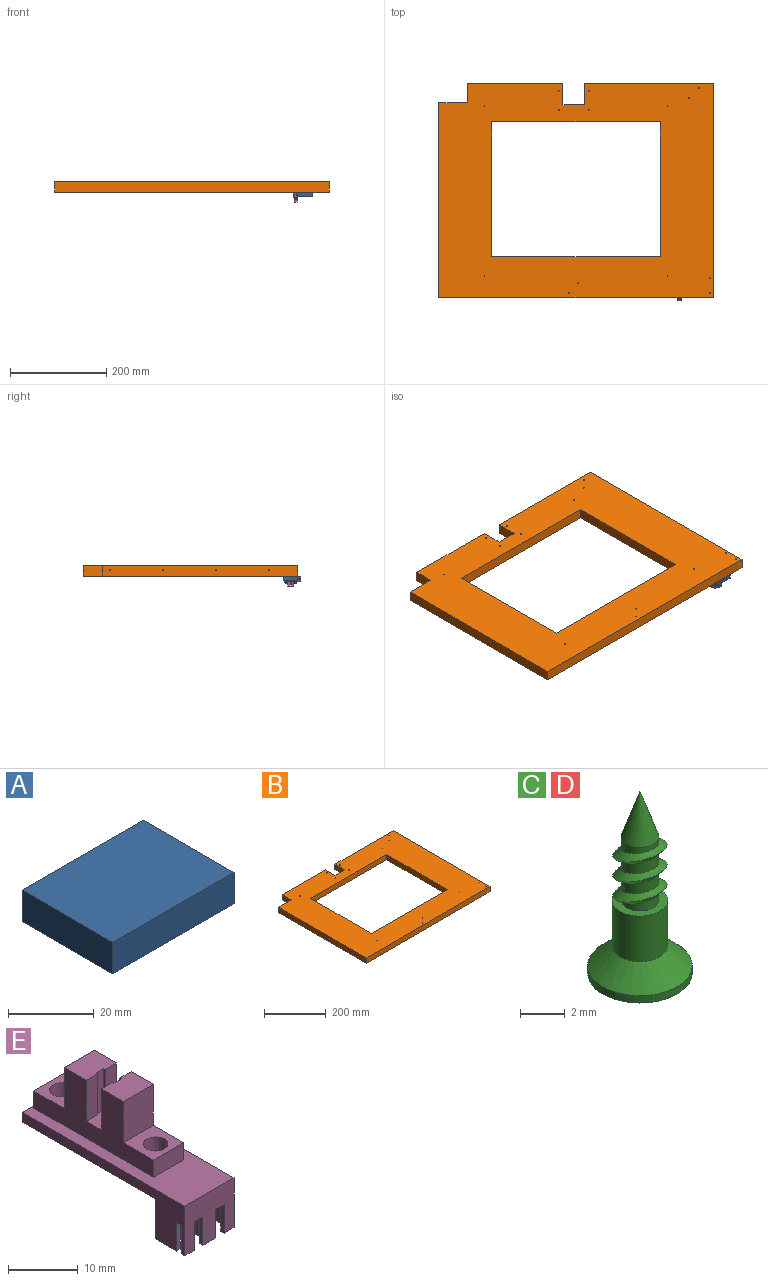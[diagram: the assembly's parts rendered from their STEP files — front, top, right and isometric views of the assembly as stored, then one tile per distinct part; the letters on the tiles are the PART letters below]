
ASSEMBLY  parts=5 mates=4
PART A: 6 faces, bbox 40x30x9 mm
  f0: plane 40x9mm, normal (0,-1,0), area 360mm2, adj f1,f3,f4,f5
  f1: plane 30x9mm, normal (-1,0,0), area 270mm2, adj f0,f2,f4,f5
  f2: plane 40x9mm, normal (0,1,0), area 360mm2, adj f1,f3,f4,f5
  f3: plane 30x9mm, normal (1,0,0), area 270mm2, adj f0,f2,f4,f5
  f4: plane 40x30mm, normal (0,0,-1), area 1200mm2, adj f0,f1,f2,f3
  f5: plane 40x30mm, normal (0,0,1), area 1200mm2, adj f0,f1,f2,f3
PART B: 72 faces, bbox 570x445x21 mm
  f0: plane 198x21mm, normal (0,1,0), area 4154.9mm2, adj f1,f2,f24,f25,f62
  f1: plane 570x445mm, normal (0,0,1), area 151270mm2, adj f0,f9,f10,f11,f12,f13,f14,f15
  f2: plane 570x445mm, normal (0,0,-1), area 149931.7mm2, adj f0,f3,f4,f5,f6,f7,f8,f9
  f3: cylinder r=8mm len=16mm, axis (0,0,-1), area 552.9mm2, adj f2,f21
  f4: cylinder r=5mm len=11mm, axis (0,0,-1), area 345.6mm2, adj f2,f20
  f5: cylinder r=8mm len=16mm, axis (0,0,-1), area 552.9mm2, adj f2,f19
  f6: cylinder r=8mm len=16mm, axis (0,0,-1), area 552.9mm2, adj f2,f18
  f7: cylinder r=5mm len=11mm, axis (0,0,-1), area 345.6mm2, adj f2,f17
  f8: cylinder r=8mm len=16mm, axis (0,0,-1), area 552.9mm2, adj f2,f16
  f9: plane 570x21mm, normal (0,-1,0), area 11970mm2, adj f1,f2,f14,f15
  f10: plane 280x21mm, normal (1,0,0), area 5880mm2, adj f1,f2,f11,f13
  f11: plane 350x21mm, normal (0,-1,0), area 7350mm2, adj f1,f2,f10,f12
  f12: plane 280x21mm, normal (-1,0,0), area 5880mm2, adj f1,f2,f11,f13
  f13: plane 350x21mm, normal (0,1,0), area 7350mm2, adj f1,f2,f10,f12
  f14: plane 405x21mm, normal (-1,0,0), area 8492.4mm2, adj f1,f2,f9,f23,f50,f52,f54,f56
  f15: plane 445x21mm, normal (1,0,0), area 9332.4mm2, adj f1,f2,f9,f22,f42,f44,f46,f48
  f16: plane 16x16mm, normal (0,0,-1), area 201.1mm2, adj f8
  f17: plane 10x10mm, normal (0,0,-1), area 78.5mm2, adj f7
  f18: plane 16x16mm, normal (0,0,-1), area 201.1mm2, adj f6
  f19: plane 16x16mm, normal (0,0,-1), area 201.1mm2, adj f5
  f20: plane 10x10mm, normal (0,0,-1), area 78.5mm2, adj f4
  f21: plane 16x16mm, normal (0,0,-1), area 201.1mm2, adj f3
  f22: plane 268x21mm, normal (0,1,0), area 5621.7mm2, adj f1,f2,f15,f27,f58,f60
  f23: plane 60x21mm, normal (0,1,0), area 1260mm2, adj f1,f2,f14,f24
  f24: plane 40x21mm, normal (-1,0,0), area 840mm2, adj f0,f1,f2,f23
  f25: plane 44x21mm, normal (1,0,0), area 924mm2, adj f0,f1,f2,f26
  f26: plane 44x21mm, normal (0,1,0), area 924mm2, adj f1,f2,f25,f27
  f27: plane 44x21mm, normal (-1,0,0), area 924mm2, adj f1,f2,f22,f26
  f28: cylinder r=1mm len=21mm, axis (0,0,-1), area 131.9mm2, adj f1,f2
  f29: cylinder r=1mm len=18mm, axis (0,0,-1), area 113.1mm2, adj f1,f69
  f30: cylinder r=1mm len=18mm, axis (0,0,-1), area 113.1mm2, adj f1,f68
  f31: cylinder r=1mm len=18mm, axis (0,0,-1), area 113.1mm2, adj f1,f64
  f32: cylinder r=1mm len=21mm, axis (0,0,-1), area 131.9mm2, adj f1,f2
  f33: cylinder r=1mm len=21mm, axis (0,0,-1), area 131.9mm2, adj f1,f2
  f34: cylinder r=1mm len=21mm, axis (0,0,-1), area 131.9mm2, adj f1,f2
  f35: cylinder r=1mm len=21mm, axis (0,0,-1), area 131.9mm2, adj f1,f2
  f36: cylinder r=1mm len=21mm, axis (0,0,-1), area 131.9mm2, adj f1,f2
  f37: cylinder r=1mm len=18mm, axis (0,0,-1), area 113.1mm2, adj f1,f66
  f38: cylinder r=1mm len=18mm, axis (0,0,-1), area 113.1mm2, adj f1,f65
  f39: cylinder r=1mm len=18mm, axis (0,0,-1), area 113.1mm2, adj f1,f67
  f40: cylinder r=1mm len=18mm, axis (0,0,-1), area 113.1mm2, adj f1,f70
  f41: cylinder r=1mm len=18mm, axis (0,0,-1), area 113.1mm2, adj f1,f71
  f42: cylinder r=1mm len=25mm, axis (1,0,0), area 157.1mm2, adj f15,f43
  f43: plane 2x2mm, normal (1,0,0), area 3.1mm2, adj f42
  f44: cylinder r=1mm len=25mm, axis (1,0,0), area 157.1mm2, adj f15,f45
  f45: plane 2x2mm, normal (1,0,0), area 3.1mm2, adj f44
  f46: cylinder r=1mm len=25mm, axis (1,0,0), area 157.1mm2, adj f15,f47
  f47: plane 2x2mm, normal (1,0,0), area 3.1mm2, adj f46
  f48: cylinder r=1mm len=25mm, axis (1,0,0), area 157.1mm2, adj f15,f49
  f49: plane 2x2mm, normal (1,0,0), area 3.1mm2, adj f48
  f50: cylinder r=1mm len=25mm, axis (-1,0,0), area 157.1mm2, adj f14,f51
  f51: plane 2x2mm, normal (-1,0,0), area 3.1mm2, adj f50
  f52: cylinder r=1mm len=25mm, axis (-1,0,0), area 157.1mm2, adj f14,f53
  f53: plane 2x2mm, normal (-1,0,0), area 3.1mm2, adj f52
  f54: cylinder r=1mm len=25mm, axis (-1,0,0), area 157.1mm2, adj f14,f55
  f55: plane 2x2mm, normal (-1,0,0), area 3.1mm2, adj f54
  f56: cylinder r=1mm len=25mm, axis (-1,0,0), area 157.1mm2, adj f14,f57
  f57: plane 2x2mm, normal (-1,0,0), area 3.1mm2, adj f56
  f58: cylinder r=1mm len=25mm, axis (0,1,0), area 157.1mm2, adj f22,f59
  f59: plane 2x2mm, normal (0,1,0), area 3.1mm2, adj f58
  f60: cylinder r=1mm len=25mm, axis (0,1,0), area 157.1mm2, adj f22,f61
  f61: plane 2x2mm, normal (0,1,0), area 3.1mm2, adj f60
  f62: cylinder r=1mm len=25mm, axis (0,1,0), area 157.1mm2, adj f0,f63
  f63: plane 2x2mm, normal (0,1,0), area 3.1mm2, adj f62
  f64: cone r=1mm half-angle=45deg, axis (0,0,-1), area 66.6mm2, adj f2,f31
  f65: cone r=1mm half-angle=45deg, axis (0,0,-1), area 66.6mm2, adj f2,f38
  f66: cone r=1mm half-angle=45deg, axis (0,0,-1), area 66.6mm2, adj f2,f37
  f67: cone r=1mm half-angle=45deg, axis (0,0,-1), area 66.6mm2, adj f2,f39
  f68: cone r=1mm half-angle=45deg, axis (0,0,-1), area 66.6mm2, adj f2,f30
  f69: cone r=1mm half-angle=45deg, axis (0,0,-1), area 66.6mm2, adj f2,f29
  f70: cone r=1mm half-angle=45deg, axis (0,0,-1), area 66.6mm2, adj f2,f40
  f71: cone r=1mm half-angle=45deg, axis (0,0,-1), area 66.6mm2, adj f2,f41
PART C: 35 faces, bbox 5.2x5.2x10.5 mm
  f0: cone r=0.42mm half-angle=18.8deg, axis (0,0,-1), area 7.1mm2, adj f11
  f1: cylinder r=0.85mm len=1.7mm, axis (0,0,1), area 1.5mm2, adj f7,f32,f34
  f2: cylinder r=1.25mm len=2.5mm, axis (0,0,1), area 19.6mm2, adj f3,f34
  f3: cone r=1.8mm half-angle=45deg, axis (0,0,-1), area 17.6mm2, adj f2,f4
  f4: cylinder r=2.35mm len=4.7mm, axis (0,0,1), area 5.9mm2, adj f3,f33
  f5: cylinder r=0.85mm len=1.7mm, axis (0,0,1), area 2.7mm2, adj f6,f10,f30,f31
  f6: cone r=1.05mm half-angle=55.5deg, axis (0,-0.31,-0.95), area 3mm2, adj f5,f7,f31
  f7: cone r=1.05mm half-angle=55.5deg, axis (0,0.31,0.95), area 3mm2, adj f1,f6,f32
  f8: cylinder r=0.85mm len=1.7mm, axis (0,0,1), area 2.7mm2, adj f9,f13,f28,f29
  f9: cone r=1.05mm half-angle=55.5deg, axis (0,-0.31,-0.95), area 3mm2, adj f8,f10,f29
  f10: cone r=1.05mm half-angle=55.5deg, axis (0,0.31,0.95), area 3mm2, adj f5,f9,f30
  f11: cylinder r=0.85mm len=1.7mm, axis (0,0,1), area 2.6mm2, adj f0,f12,f27
  f12: cone r=1.05mm half-angle=55.5deg, axis (0,-0.31,-0.95), area 3mm2, adj f11,f13,f27
  f13: cone r=1.05mm half-angle=55.5deg, axis (0,0.31,0.95), area 3mm2, adj f8,f12,f28
  f14: plane 1.48x0.7mm, normal (0,0.98,-0.17), area 0.7mm2, adj f15,f25,f26,f33
  f15: plane 1.48x1.31mm, normal (0.98,0,-0.17), area 1.6mm2, adj f14,f16,f26,f33
  f16: plane 1.48x1.31mm, normal (0,0.98,-0.17), area 1.6mm2, adj f15,f17,f26,f33
  f17: plane 1.48x0.7mm, normal (0.98,0,-0.17), area 0.7mm2, adj f16,f18,f26,f33
  f18: plane 1.48x1.31mm, normal (0,-0.98,-0.17), area 1.6mm2, adj f17,f19,f26,f33
  f19: plane 1.48x1.31mm, normal (0.98,0,-0.17), area 1.6mm2, adj f18,f20,f26,f33
  f20: plane 1.48x0.7mm, normal (0,-0.98,-0.17), area 0.7mm2, adj f19,f21,f26,f33
  f21: plane 1.48x1.31mm, normal (-0.98,0,-0.17), area 1.6mm2, adj f20,f22,f26,f33
  f22: plane 1.48x1.31mm, normal (0,-0.98,-0.17), area 1.6mm2, adj f21,f23,f26,f33
  f23: plane 1.48x0.7mm, normal (-0.98,0,-0.17), area 0.7mm2, adj f22,f24,f26,f33
  f24: plane 1.48x1.31mm, normal (0,0.98,-0.17), area 1.6mm2, adj f23,f25,f26,f33
  f25: plane 1.48x1.31mm, normal (-0.98,0,-0.17), area 1.6mm2, adj f14,f24,f26,f33
  f26: plane 2.28x2.28mm, normal (0,0,-1), area 0.8mm2, adj f14,f15,f16,f17,f18,f19,f20,f21
  f27: plane 1.81x0.96mm, normal (0,0.31,0.95), area 0.1mm2, adj f11,f12
  f28: plane 2.22x1.37mm, normal (0,-0.31,-0.95), area 0.1mm2, adj f8,f13
  f29: plane 1.81x0.96mm, normal (0,0.31,0.95), area 0.1mm2, adj f8,f9
  f30: plane 2.22x1.37mm, normal (0,-0.31,-0.95), area 0.1mm2, adj f5,f10
  f31: plane 1.81x0.96mm, normal (0,0.31,0.95), area 0.1mm2, adj f5,f6
  f32: plane 1.7x0.85mm, normal (0,-0.31,-0.95), area 0.1mm2, adj f1,f7
  f33: plane 4.7x4.7mm, normal (0,0,-1), area 13.9mm2, adj f4,f14,f15,f16,f17,f18,f19,f20
  f34: plane 2.5x2.5mm, normal (0,0,1), area 2.6mm2, adj f1,f2
PART D: same geometry as C
PART E: 74 faces, bbox 10x33x18.9 mm
  f0: plane 0.2x0.2mm, normal (0,0,-1), area 0mm2, adj f56,f57,f58,f59
  f1: plane 0.6x0.2mm, normal (-0.71,0,-0.71), area 0.1mm2, adj f50,f51,f70,f72
  f2: plane 0.2x0.2mm, normal (0,0,-1), area 0mm2, adj f52,f53,f54,f55
  f3: plane 10x4.35mm, normal (0,0,-1), area 12.1mm2, adj f27,f32,f38,f39,f40,f41,f42,f47
  f4: plane 6.15x6.1mm, normal (0,0,1), area 27.9mm2, adj f8,f9,f10,f11,f25
  f5: plane 6.15x6.1mm, normal (0,0,1), area 27.9mm2, adj f8,f9,f12,f18,f73
  f6: plane 6.1x3.6mm, normal (0,0,1), area 19.2mm2, adj f7,f8,f9,f14,f15,f16,f17,f20
  f7: plane 7.2x2.3mm, normal (0,-1,0), area 16.6mm2, adj f6,f9,f14,f19
  f8: plane 24.3x10.2mm, normal (1,0,0), area 137.7mm2, adj f4,f5,f6,f10,f13,f17,f18,f19
  f9: plane 24.3x10.2mm, normal (-1,0,0), area 137.7mm2, adj f4,f5,f6,f7,f10,f13,f18,f19
  f10: plane 6.1x3mm, normal (0,-1,0), area 18.3mm2, adj f4,f8,f9,f13
  f11: cylinder r=1.75mm len=4.7mm, axis (0,0,1), area 51.7mm2, adj f4,f30
  f12: cylinder r=1.75mm len=4.7mm, axis (0,0,1), area 51.7mm2, adj f5,f30
  f13: plane 33x10mm, normal (0,0,1), area 181.8mm2, adj f8,f9,f10,f27,f31,f32,f33,f73
  f14: plane 7.2x0.3mm, normal (1,0,0), area 2.2mm2, adj f6,f7,f15,f19
  f15: plane 7.2x1.5mm, normal (0,-1,0), area 10.8mm2, adj f6,f14,f16,f19
  f16: plane 7.2x0.3mm, normal (-1,0,0), area 2.2mm2, adj f6,f15,f17,f19
  f17: plane 7.2x2.3mm, normal (0,-1,0), area 16.6mm2, adj f6,f8,f16,f19
  f18: plane 7.2x6.1mm, normal (0,1,0), area 43.9mm2, adj f5,f8,f9,f19
  f19: plane 6.1x4.5mm, normal (0,0,1), area 27mm2, adj f7,f8,f9,f14,f15,f16,f17,f18
  f20: plane 7.2x2.3mm, normal (0,1,0), area 16.6mm2, adj f6,f8,f21,f26
  f21: plane 7.2x0.3mm, normal (-1,0,0), area 2.2mm2, adj f6,f20,f22,f26
  f22: plane 7.2x1.5mm, normal (0,1,0), area 10.8mm2, adj f6,f21,f23,f26
  f23: plane 7.2x0.3mm, normal (1,0,0), area 2.2mm2, adj f6,f22,f24,f26
  f24: plane 7.2x2.3mm, normal (0,1,0), area 16.6mm2, adj f6,f9,f23,f26
  f25: plane 7.2x6.1mm, normal (0,-1,0), area 43.9mm2, adj f4,f8,f9,f26
  f26: plane 6.1x4.5mm, normal (0,0,1), area 27mm2, adj f8,f9,f20,f21,f22,f23,f24,f25
  f27: plane 33x8.7mm, normal (1,0,0), area 93.3mm2, adj f3,f13,f28,f30,f31,f33,f38,f43
  f28: plane 2x0.7mm, normal (0,0,-1), area 1.4mm2, adj f27,f33,f35,f43
  f29: plane 2.6x0.7mm, normal (0,0,-1), area 1.8mm2, adj f33,f34,f36,f44
  f30: plane 27x10mm, normal (0,0,-1), area 250.8mm2, adj f11,f12,f27,f31,f32,f47
  f31: plane 10x1.7mm, normal (0,1,0), area 17mm2, adj f13,f27,f30,f32
  f32: plane 33x8.7mm, normal (-1,0,0), area 93.3mm2, adj f3,f13,f30,f31,f33,f39,f45,f46
  f33: plane 10x8.7mm, normal (0,-1,0), area 70mm2, adj f13,f27,f28,f29,f32,f34,f35,f36
  f34: plane 5x0.7mm, normal (1,0,0), area 3.5mm2, adj f29,f33,f44,f46
  f35: plane 5x0.7mm, normal (-1,0,0), area 3.5mm2, adj f28,f33,f43,f46
  f36: plane 5x0.7mm, normal (-1,0,0), area 3.5mm2, adj f29,f33,f44,f46
  f37: plane 5x0.7mm, normal (1,0,0), area 3.5mm2, adj f33,f45,f46,f48
  f38: plane 5x0.7mm, normal (0,-1,0), area 3.5mm2, adj f3,f27,f40,f46
  f39: plane 5x0.7mm, normal (0,-1,0), area 3.5mm2, adj f3,f32,f41,f46
  f40: plane 5x3.65mm, normal (-1,0,0), area 18.3mm2, adj f3,f38,f42,f46
  f41: plane 5x3.65mm, normal (1,0,0), area 18.3mm2, adj f3,f39,f42,f46
  f42: plane 8.6x5mm, normal (0,-1,0), area 43mm2, adj f3,f40,f41,f46
  f43: plane 5x2mm, normal (0,1,0), area 10mm2, adj f27,f28,f35,f46
  f44: plane 5x2.6mm, normal (0,1,0), area 13mm2, adj f29,f34,f36,f46
  f45: plane 5x2mm, normal (0,1,0), area 10mm2, adj f32,f37,f46,f48
  f46: plane 10x5.3mm, normal (0,0,-1), area 42.2mm2, adj f27,f32,f33,f34,f35,f36,f37,f38
  f47: plane 10x7mm, normal (0,1,0), area 70mm2, adj f3,f27,f30,f32
  f48: plane 2x0.7mm, normal (0,0,-1), area 1.4mm2, adj f32,f33,f37,f45
  f49: plane 0.6x0.2mm, normal (0.71,0,-0.71), area 0.1mm2, adj f50,f51,f71,f72
  f50: plane 0.6x0.2mm, normal (0,0.71,-0.71), area 0.1mm2, adj f1,f49,f69,f72
  f51: plane 0.6x0.2mm, normal (0,-0.71,-0.71), area 0.1mm2, adj f1,f49,f68,f72
  f52: plane 0.6x0.2mm, normal (0.71,0,-0.71), area 0.1mm2, adj f2,f53,f54,f67
  f53: plane 0.6x0.2mm, normal (0,0.71,-0.71), area 0.1mm2, adj f2,f52,f55,f65
  f54: plane 0.6x0.2mm, normal (0,-0.71,-0.71), area 0.1mm2, adj f2,f52,f55,f64
  f55: plane 0.6x0.2mm, normal (-0.71,0,-0.71), area 0.1mm2, adj f2,f53,f54,f66
  f56: plane 0.6x0.2mm, normal (-0.71,0,-0.71), area 0.1mm2, adj f0,f57,f58,f62
  f57: plane 0.6x0.2mm, normal (0,0.71,-0.71), area 0.1mm2, adj f0,f56,f59,f61
  f58: plane 0.6x0.2mm, normal (0,-0.71,-0.71), area 0.1mm2, adj f0,f56,f59,f60
  f59: plane 0.6x0.2mm, normal (0.71,0,-0.71), area 0.1mm2, adj f0,f57,f58,f63
  f60: plane 4.8x0.6mm, normal (0,-1,0), area 2.9mm2, adj f46,f58,f62,f63
  f61: plane 4.8x0.6mm, normal (0,1,0), area 2.9mm2, adj f46,f57,f62,f63
  f62: plane 4.8x0.6mm, normal (-1,0,0), area 2.9mm2, adj f46,f56,f60,f61
  f63: plane 4.8x0.6mm, normal (1,0,0), area 2.9mm2, adj f46,f59,f60,f61
  f64: plane 4.8x0.6mm, normal (0,-1,0), area 2.9mm2, adj f46,f54,f66,f67
  f65: plane 4.8x0.6mm, normal (0,1,0), area 2.9mm2, adj f46,f53,f66,f67
  f66: plane 4.8x0.6mm, normal (-1,0,0), area 2.9mm2, adj f46,f55,f64,f65
  f67: plane 4.8x0.6mm, normal (1,0,0), area 2.9mm2, adj f46,f52,f64,f65
  f68: plane 4.8x0.6mm, normal (0,-1,0), area 2.9mm2, adj f46,f51,f70,f71
  f69: plane 4.8x0.6mm, normal (0,1,0), area 2.9mm2, adj f46,f50,f70,f71
  f70: plane 4.8x0.6mm, normal (-1,0,0), area 2.9mm2, adj f1,f46,f68,f69
  f71: plane 4.8x0.6mm, normal (1,0,0), area 2.9mm2, adj f46,f49,f68,f69
  f72: plane 0.2x0.2mm, normal (0,0,-1), area 0mm2, adj f1,f49,f50,f51
  f73: plane 6.1x3mm, normal (0,1,0), area 18.3mm2, adj f5,f8,f9,f13
PLACE A rot(axis=(1,0,0),180deg) t=(114.15,-567.92,801)mm
PLACE B t=(84.15,-147.92,-215)mm
PLACE C t=(299.15,-349.02,282.3)mm
PLACE D t=(299.15,-368.02,282.3)mm
PLACE E rot(axis=(0,1,0),180deg) t=(258.69,-339.69,288.5)mm
MATE fastened B.f2 <-> A.f4  axis (0,0,-1) through (369.15,-372.92,297.5)mm
MATE fastened E.f30 <-> A.f5  axis (0,0,1) through (294.15,-372.92,288.5)mm
MATE fastened C.f2 <-> E.f12  axis (0,0,1) through (299.15,-349.02,283.8)mm
MATE fastened D.f2 <-> E.f11  axis (0,0,1) through (299.15,-368.02,283.8)mm
